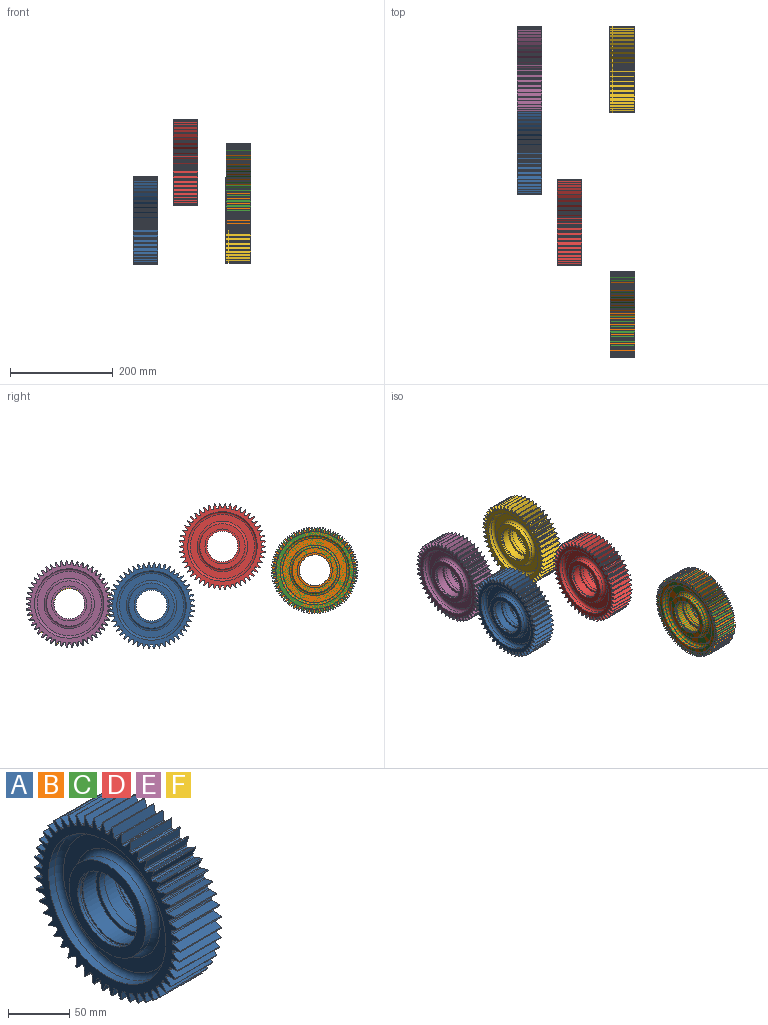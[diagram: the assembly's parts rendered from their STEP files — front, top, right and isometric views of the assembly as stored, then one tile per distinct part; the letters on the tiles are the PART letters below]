
ASSEMBLY  parts=6 mates=1
PART A: 327 faces, bbox 48x168x167.7 mm
  f0: plane 168x167.74mm, normal (-1,0,0), area 5101.1mm2, adj f1,f2,f3,f4,f5,f6,f7,f8
  f1: cylinder r=84mm len=48mm, axis (-1,0,0), area 45.2mm2, adj f0,f51,f122,f156
  f2: cylinder r=84mm len=48mm, axis (-1,0,0), area 43.9mm2, adj f0,f51,f151,f152
  f3: cylinder r=84mm len=48mm, axis (-1,0,0), area 42.7mm2, adj f0,f51,f147,f166
  f4: cylinder r=84mm len=48mm, axis (-1,0,0), area 41.5mm2, adj f0,f51,f161,f162
  f5: cylinder r=84mm len=48mm, axis (-1,0,0), area 40.5mm2, adj f0,f51,f136,f157
  f6: cylinder r=84mm len=48mm, axis (-1,0,0), area 39.7mm2, adj f0,f51,f131,f132
  f7: cylinder r=84mm len=48mm, axis (-1,0,0), area 39mm2, adj f0,f51,f127,f141
  f8: cylinder r=84mm len=48mm, axis (-1,0,0), area 38.4mm2, adj f0,f51,f137,f146
  f9: cylinder r=84mm len=48mm, axis (-1,0,0), area 38.1mm2, adj f0,f51,f86,f142
  f10: cylinder r=84mm len=48mm, axis (-1,0,0), area 37.9mm2, adj f0,f51,f80,f82
  f11: cylinder r=84mm len=48mm, axis (-1,0,0), area 38.1mm2, adj f0,f51,f207,f216
  f12: cylinder r=84mm len=48mm, axis (-1,0,0), area 38.4mm2, adj f0,f51,f212,f226
  f13: cylinder r=84mm len=48mm, axis (-1,0,0), area 39mm2, adj f0,f51,f221,f222
  f14: cylinder r=84mm len=48mm, axis (-1,0,0), area 39.7mm2, adj f0,f51,f217,f241
  f15: cylinder r=84mm len=48mm, axis (-1,0,0), area 40.6mm2, adj f0,f51,f237,f246
  f16: cylinder r=84mm len=48mm, axis (-1,0,0), area 41.6mm2, adj f0,f51,f231,f242
  f17: cylinder r=84mm len=48mm, axis (-1,0,0), area 42.7mm2, adj f0,f51,f227,f236
  f18: cylinder r=84mm len=48mm, axis (-1,0,0), area 43.9mm2, adj f0,f51,f206,f232
  f19: cylinder r=84mm len=48mm, axis (-1,0,0), area 45.2mm2, adj f0,f51,f201,f202
  f20: cylinder r=84mm len=48mm, axis (-1,0,0), area 46.6mm2, adj f0,f51,f196,f197
  f21: cylinder r=84mm len=48mm, axis (-1,0,0), area 48mm2, adj f0,f51,f191,f192
  f22: cylinder r=84mm len=48mm, axis (-1,0,0), area 49.5mm2, adj f0,f51,f186,f187
  f23: cylinder r=84mm len=48mm, axis (-1,0,0), area 50.9mm2, adj f0,f51,f181,f182
  f24: cylinder r=84mm len=48mm, axis (-1,0,0), area 52.4mm2, adj f0,f51,f171,f177
  f25: cylinder r=84mm len=48mm, axis (-1,0,0), area 53.8mm2, adj f0,f51,f167,f176
  f26: cylinder r=84mm len=48mm, axis (-1,0,0), area 55.1mm2, adj f0,f51,f172,f276
  f27: cylinder r=84mm len=48mm, axis (-1,0,0), area 56.3mm2, adj f0,f51,f271,f272
  f28: cylinder r=84mm len=48mm, axis (-1,0,0), area 57.4mm2, adj f0,f51,f267,f286
  f29: cylinder r=84mm len=48mm, axis (-1,0,0), area 58.4mm2, adj f0,f51,f281,f282
  f30: cylinder r=84mm len=48mm, axis (-1,0,0), area 59.3mm2, adj f0,f51,f261,f277
  f31: cylinder r=84mm len=48mm, axis (-1,0,0), area 60mm2, adj f0,f51,f257,f266
  f32: cylinder r=84mm len=48mm, axis (-1,0,0), area 60.5mm2, adj f0,f51,f256,f262
  f33: cylinder r=84mm len=48mm, axis (-1,0,0), area 60.8mm2, adj f0,f51,f251,f252
  f34: cylinder r=84mm len=48mm, axis (-1,0,0), area 61mm2, adj f0,f51,f247,f326
  f35: cylinder r=84mm len=48mm, axis (-1,0,0), area 61mm2, adj f0,f51,f321,f322
  f36: cylinder r=84mm len=48mm, axis (-1,0,0), area 60.8mm2, adj f0,f51,f316,f317
  f37: cylinder r=84mm len=48mm, axis (-1,0,0), area 60.5mm2, adj f0,f51,f311,f312
  f38: cylinder r=84mm len=48mm, axis (-1,0,0), area 59.9mm2, adj f0,f51,f296,f307
  f39: cylinder r=84mm len=48mm, axis (-1,0,0), area 59.2mm2, adj f0,f51,f291,f292
  f40: cylinder r=84mm len=48mm, axis (-1,0,0), area 58.4mm2, adj f0,f51,f287,f306
  f41: cylinder r=84mm len=48mm, axis (-1,0,0), area 57.4mm2, adj f0,f51,f301,f302
  f42: cylinder r=84mm len=48mm, axis (-1,0,0), area 56.3mm2, adj f0,f51,f96,f297
  f43: cylinder r=84mm len=48mm, axis (-1,0,0), area 55.1mm2, adj f0,f51,f91,f92
  f44: cylinder r=84mm len=48mm, axis (-1,0,0), area 53.7mm2, adj f0,f51,f87,f101
  f45: cylinder r=84mm len=48mm, axis (-1,0,0), area 52.4mm2, adj f0,f51,f97,f106
  f46: cylinder r=84mm len=48mm, axis (-1,0,0), area 50.9mm2, adj f0,f51,f102,f111
  f47: cylinder r=84mm len=48mm, axis (-1,0,0), area 49.5mm2, adj f0,f51,f107,f116
  f48: cylinder r=84mm len=48mm, axis (-1,0,0), area 48mm2, adj f0,f51,f112,f121
  f49: cylinder r=84mm len=48mm, axis (-1,0,0), area 46.6mm2, adj f0,f51,f117,f126
  f50: cylinder r=84mm len=48mm, axis (-1,0,0), area 37.9mm2, adj f0,f51,f81,f211
  f51: plane 168x167.74mm, normal (1,0,0), area 5101.1mm2, adj f1,f2,f3,f4,f5,f6,f7,f8
  f52: cylinder r=44mm len=88mm, axis (-1,0,0), area 1935.2mm2, adj f53,f76
  f53: plane 88x88mm, normal (-1,0,0), area 2450.4mm2, adj f52,f54
  f54: cylinder r=34mm len=68mm, axis (-1,0,0), area 640.9mm2, adj f53,f55
  f55: plane 71x71mm, normal (1,0,0), area 327.5mm2, adj f54,f56
  f56: cylinder r=35.5mm len=71mm, axis (-1,0,0), area 669.2mm2, adj f55,f57
  f57: plane 71x71mm, normal (-1,0,0), area 327.5mm2, adj f56,f58
  f58: cylinder r=34mm len=68mm, axis (-1,0,0), area 3204.4mm2, adj f57,f59
  f59: plane 68x68mm, normal (-1,0,0), area 804.2mm2, adj f58,f60
  f60: cylinder r=30mm len=60mm, axis (-1,0,0), area 1131mm2, adj f59,f61
  f61: plane 68x68mm, normal (1,0,0), area 804.2mm2, adj f60,f62
  f62: cylinder r=34mm len=68mm, axis (-1,0,0), area 3204.4mm2, adj f61,f63
  f63: plane 71x71mm, normal (1,0,0), area 327.5mm2, adj f62,f64
  f64: cylinder r=35.5mm len=71mm, axis (-1,0,0), area 669.2mm2, adj f63,f65
  f65: plane 71x71mm, normal (-1,0,0), area 327.5mm2, adj f64,f66
  f66: cylinder r=34mm len=68mm, axis (-1,0,0), area 640.9mm2, adj f65,f67
  f67: plane 88x88mm, normal (1,0,0), area 2450.4mm2, adj f66,f68
  f68: cylinder r=44mm len=88mm, axis (-1,0,0), area 2535.7mm2, adj f67,f69
  f69: torus R=46.83mm, axis (-1,0,0), area 1256.8mm2, adj f68,f70
  f70: plane 125x125mm, normal (1,0,0), area 5382.8mm2, adj f69,f71
  f71: torus R=62.5mm, axis (-1,0,0), area 3241.3mm2, adj f70,f72
  f72: cylinder r=67.5mm len=135mm, axis (-1,0,0), area 2968.8mm2, adj f51,f71
  f73: cylinder r=67.5mm len=135mm, axis (-1,0,0), area 2968.8mm2, adj f0,f74
  f74: torus R=62.5mm, axis (-1,0,0), area 3241.3mm2, adj f73,f75
  f75: plane 125x125mm, normal (-1,0,0), area 4728.9mm2, adj f74,f76
  f76: torus R=49mm, axis (-1,0,0), area 2261mm2, adj f52,f75
  f77: cylinder r=1mm len=48mm, axis (-1,0,0), area 58.6mm2, adj f0,f51,f78,f81
  f78: plane 48x1.77mm, normal (0,0,1), area 84.8mm2, adj f0,f51,f77,f79
  f79: cylinder r=1mm len=48mm, axis (-1,0,0), area 58.8mm2, adj f0,f51,f78,f80
  f80: plane 48x8.31mm, normal (0,-0.94,0.34), area 423.7mm2, adj f0,f10,f51,f79
  f81: plane 48x8.3mm, normal (0,0.93,0.36), area 426.6mm2, adj f0,f50,f51,f77
  f82: plane 48x8.63mm, normal (0,0.97,0.24), area 426.6mm2, adj f0,f10,f51,f83
  f83: cylinder r=1mm len=48mm, axis (-1,0,0), area 58.6mm2, adj f0,f51,f82,f84
  f84: plane 48x1.75mm, normal (0,0.13,0.99), area 84.8mm2, adj f0,f51,f83,f85
  f85: cylinder r=1mm len=48mm, axis (-1,0,0), area 58.8mm2, adj f0,f51,f84,f86
  f86: plane 48x7.86mm, normal (0,-0.89,0.45), area 423.4mm2, adj f0,f9,f51,f85
  f87: plane 48x8.29mm, normal (0,-0.07,-1), area 398.9mm2, adj f0,f44,f51,f88
  f88: cylinder r=1mm len=48mm, axis (-1,0,0), area 58.6mm2, adj f0,f51,f87,f89
  f89: plane 48x1.6mm, normal (0,0.9,-0.43), area 84.8mm2, adj f0,f51,f88,f90
  f90: cylinder r=1mm len=48mm, axis (-1,0,0), area 58.8mm2, adj f0,f51,f89,f91
  f91: plane 48x5.81mm, normal (0,0.71,0.71), area 394.2mm2, adj f0,f43,f51,f90
  f92: plane 48x8.1mm, normal (0,-0.2,-0.98), area 396.6mm2, adj f0,f43,f51,f93
  f93: cylinder r=1mm len=48mm, axis (-1,0,0), area 58.6mm2, adj f0,f51,f92,f94
  f94: plane 48x1.49mm, normal (0,0.84,-0.54), area 84.8mm2, adj f0,f51,f93,f95
  f95: cylinder r=1mm len=48mm, axis (-1,0,0), area 58.8mm2, adj f0,f51,f94,f96
  f96: plane 48x6.45mm, normal (0,0.79,0.61), area 392mm2, adj f0,f42,f51,f95
  f97: plane 48x8.35mm, normal (0,0.05,-1), area 401.3mm2, adj f0,f45,f51,f98
  f98: cylinder r=1mm len=48mm, axis (-1,0,0), area 58.6mm2, adj f0,f51,f97,f99
  f99: plane 48x1.68mm, normal (0,0.95,-0.31), area 84.8mm2, adj f0,f51,f98,f100
  f100: cylinder r=1mm len=48mm, axis (-1,0,0), area 58.8mm2, adj f0,f51,f99,f101
  f101: plane 48x6.53mm, normal (0,0.61,0.79), area 396.4mm2, adj f0,f44,f51,f100
  f102: plane 48x8.28mm, normal (0,0.18,-0.98), area 403.8mm2, adj f0,f46,f51,f103
  f103: cylinder r=1mm len=48mm, axis (-1,0,0), area 58.6mm2, adj f0,f51,f102,f104
  f104: plane 48x1.74mm, normal (0,0.98,-0.19), area 84.8mm2, adj f0,f51,f103,f105
  f105: cylinder r=1mm len=48mm, axis (-1,0,0), area 58.8mm2, adj f0,f51,f104,f106
  f106: plane 48x7.15mm, normal (0,0.51,0.86), area 398.8mm2, adj f0,f45,f51,f105
  f107: plane 48x8.08mm, normal (0,0.3,-0.95), area 406.3mm2, adj f0,f47,f51,f108
  f108: cylinder r=1mm len=48mm, axis (-1,0,0), area 58.6mm2, adj f0,f51,f107,f109
  f109: plane 48x1.76mm, normal (0,1,-0.06), area 84.8mm2, adj f0,f51,f108,f110
  f110: cylinder r=1mm len=48mm, axis (-1,0,0), area 58.8mm2, adj f0,f51,f109,f111
  f111: plane 48x7.67mm, normal (0,0.4,0.92), area 401.3mm2, adj f0,f46,f51,f110
  f112: plane 48x7.75mm, normal (0,0.42,-0.91), area 408.9mm2, adj f0,f48,f51,f113
  f113: cylinder r=1mm len=48mm, axis (-1,0,0), area 58.6mm2, adj f0,f51,f112,f114
  f114: plane 48x1.76mm, normal (0,1,0.06), area 84.8mm2, adj f0,f51,f113,f115
  f115: cylinder r=1mm len=48mm, axis (-1,0,0), area 58.8mm2, adj f0,f51,f114,f116
  f116: plane 48x8.08mm, normal (0,0.28,0.96), area 403.8mm2, adj f0,f47,f51,f115
  f117: plane 48x7.29mm, normal (0,0.53,-0.85), area 411.4mm2, adj f0,f49,f51,f118
  f118: cylinder r=1mm len=48mm, axis (-1,0,0), area 58.6mm2, adj f0,f51,f117,f119
  f119: plane 48x1.74mm, normal (0,0.98,0.19), area 84.8mm2, adj f0,f51,f118,f120
  f120: cylinder r=1mm len=48mm, axis (-1,0,0), area 58.8mm2, adj f0,f51,f119,f121
  f121: plane 48x8.36mm, normal (0,0.16,0.99), area 406.3mm2, adj f0,f48,f51,f120
  f122: plane 48x6.7mm, normal (0,0.63,-0.78), area 413.8mm2, adj f0,f1,f51,f123
  f123: cylinder r=1mm len=48mm, axis (-1,0,0), area 58.6mm2, adj f0,f51,f122,f124
  f124: plane 48x1.68mm, normal (0,0.95,0.31), area 84.8mm2, adj f0,f51,f123,f125
  f125: cylinder r=1mm len=48mm, axis (-1,0,0), area 58.8mm2, adj f0,f51,f124,f126
  f126: plane 48x8.51mm, normal (0,0.03,1), area 408.8mm2, adj f0,f49,f51,f125
  f127: plane 48x8.76mm, normal (0,0.99,-0.14), area 424.7mm2, adj f0,f7,f51,f128
  f128: cylinder r=1mm len=48mm, axis (-1,0,0), area 58.6mm2, adj f0,f51,f127,f129
  f129: plane 48x1.55mm, normal (0,0.48,0.88), area 84.8mm2, adj f0,f51,f128,f130
  f130: cylinder r=1mm len=48mm, axis (-1,0,0), area 58.8mm2, adj f0,f51,f129,f131
  f131: plane 48x6.57mm, normal (0,-0.66,0.75), area 420.7mm2, adj f0,f6,f51,f130
  f132: plane 48x8.52mm, normal (0,0.97,-0.26), area 423.4mm2, adj f0,f6,f51,f133
  f133: cylinder r=1mm len=48mm, axis (-1,0,0), area 58.6mm2, adj f0,f51,f132,f134
  f134: plane 48x1.43mm, normal (0,0.59,0.81), area 84.8mm2, adj f0,f51,f133,f135
  f135: cylinder r=1mm len=48mm, axis (-1,0,0), area 58.8mm2, adj f0,f51,f134,f136
  f136: plane 48x7.22mm, normal (0,-0.56,0.83), area 419.2mm2, adj f0,f5,f51,f135
  f137: plane 48x8.87mm, normal (0,1,-0.01), area 425.6mm2, adj f0,f8,f51,f138
  f138: cylinder r=1mm len=48mm, axis (-1,0,0), area 58.6mm2, adj f0,f51,f137,f139
  f139: plane 48x1.64mm, normal (0,0.37,0.93), area 84.8mm2, adj f0,f51,f138,f140
  f140: cylinder r=1mm len=48mm, axis (-1,0,0), area 58.8mm2, adj f0,f51,f139,f141
  f141: plane 48x6.6mm, normal (0,-0.75,0.66), area 421.9mm2, adj f0,f7,f51,f140
  f142: plane 48x8.82mm, normal (0,0.99,0.11), area 426.3mm2, adj f0,f9,f51,f143
  f143: cylinder r=1mm len=48mm, axis (-1,0,0), area 58.6mm2, adj f0,f51,f142,f144
  f144: plane 48x1.71mm, normal (0,0.25,0.97), area 84.8mm2, adj f0,f51,f143,f145
  f145: cylinder r=1mm len=48mm, axis (-1,0,0), area 58.8mm2, adj f0,f51,f144,f146
  f146: plane 48x7.29mm, normal (0,-0.83,0.56), area 422.8mm2, adj f0,f8,f51,f145
  f147: plane 48x6.99mm, normal (0,0.8,-0.6), area 418.2mm2, adj f0,f3,f51,f148
  f148: cylinder r=1mm len=48mm, axis (-1,0,0), area 58.6mm2, adj f0,f51,f147,f149
  f149: plane 48x1.49mm, normal (0,0.84,0.54), area 84.8mm2, adj f0,f51,f148,f150
  f150: cylinder r=1mm len=48mm, axis (-1,0,0), area 58.8mm2, adj f0,f51,f149,f151
  f151: plane 48x8.41mm, normal (0,-0.22,0.98), area 413.4mm2, adj f0,f2,f51,f150
  f152: plane 48x6.25mm, normal (0,0.72,-0.69), area 416.1mm2, adj f0,f2,f51,f153
  f153: cylinder r=1mm len=48mm, axis (-1,0,0), area 58.6mm2, adj f0,f51,f152,f154
  f154: plane 48x1.6mm, normal (0,0.9,0.43), area 84.8mm2, adj f0,f51,f153,f155
  f155: cylinder r=1mm len=48mm, axis (-1,0,0), area 58.8mm2, adj f0,f51,f154,f156
  f156: plane 48x8.53mm, normal (0,-0.09,1), area 411.2mm2, adj f0,f1,f51,f155
  f157: plane 48x8.14mm, normal (0,0.93,-0.38), area 421.9mm2, adj f0,f5,f51,f158
  f158: cylinder r=1mm len=48mm, axis (-1,0,0), area 58.6mm2, adj f0,f51,f157,f159
  f159: plane 48x1.29mm, normal (0,0.68,0.73), area 84.8mm2, adj f0,f51,f158,f160
  f160: cylinder r=1mm len=48mm, axis (-1,0,0), area 58.8mm2, adj f0,f51,f159,f161
  f161: plane 48x7.75mm, normal (0,-0.45,0.89), area 417.5mm2, adj f0,f4,f51,f160
  f162: plane 48x7.62mm, normal (0,0.87,-0.49), area 420.2mm2, adj f0,f4,f51,f163
  f163: cylinder r=1mm len=48mm, axis (-1,0,0), area 58.6mm2, adj f0,f51,f162,f164
  f164: plane 48x1.36mm, normal (0,0.77,0.64), area 84.8mm2, adj f0,f51,f163,f165
  f165: cylinder r=1mm len=48mm, axis (-1,0,0), area 58.8mm2, adj f0,f51,f164,f166
  f166: plane 48x8.14mm, normal (0,-0.34,0.94), area 415.6mm2, adj f0,f3,f51,f165
  f167: plane 48x6.47mm, normal (0,-0.63,0.78), area 399.1mm2, adj f0,f25,f51,f168
  f168: cylinder r=1mm len=48mm, axis (-1,0,0), area 58.6mm2, adj f0,f51,f167,f169
  f169: plane 48x1.68mm, normal (0,-0.95,-0.31), area 84.8mm2, adj f0,f51,f168,f170
  f170: cylinder r=1mm len=48mm, axis (-1,0,0), area 58.8mm2, adj f0,f51,f169,f171
  f171: plane 48x8.3mm, normal (0,-0.03,-1), area 398.6mm2, adj f0,f24,f51,f170
  f172: plane 48x5.96mm, normal (0,-0.72,0.69), area 396.8mm2, adj f0,f26,f51,f173
  f173: cylinder r=1mm len=48mm, axis (-1,0,0), area 58.6mm2, adj f0,f51,f172,f174
  f174: plane 48x1.6mm, normal (0,-0.9,-0.43), area 84.8mm2, adj f0,f51,f173,f175
  f175: cylinder r=1mm len=48mm, axis (-1,0,0), area 58.8mm2, adj f0,f51,f174,f176
  f176: plane 48x8.22mm, normal (0,0.09,-1), area 396.2mm2, adj f0,f25,f51,f175
  f177: plane 48x7.11mm, normal (0,-0.53,0.85), area 401.5mm2, adj f0,f24,f51,f178
  f178: cylinder r=1mm len=48mm, axis (-1,0,0), area 58.6mm2, adj f0,f51,f177,f179
  f179: plane 48x1.74mm, normal (0,-0.98,-0.19), area 84.8mm2, adj f0,f51,f178,f180
  f180: cylinder r=1mm len=48mm, axis (-1,0,0), area 58.8mm2, adj f0,f51,f179,f181
  f181: plane 48x8.25mm, normal (0,-0.16,-0.99), area 401mm2, adj f0,f23,f51,f180
  f182: plane 48x7.66mm, normal (0,-0.42,0.91), area 404mm2, adj f0,f23,f51,f183
  f183: cylinder r=1mm len=48mm, axis (-1,0,0), area 58.6mm2, adj f0,f51,f182,f184
  f184: plane 48x1.76mm, normal (0,-1,-0.06), area 84.8mm2, adj f0,f51,f183,f185
  f185: cylinder r=1mm len=48mm, axis (-1,0,0), area 58.8mm2, adj f0,f51,f184,f186
  f186: plane 48x8.07mm, normal (0,-0.28,-0.96), area 403.5mm2, adj f0,f22,f51,f185
  f187: plane 48x8.08mm, normal (0,-0.3,0.95), area 406.5mm2, adj f0,f22,f51,f188
  f188: cylinder r=1mm len=48mm, axis (-1,0,0), area 58.6mm2, adj f0,f51,f187,f189
  f189: plane 48x1.76mm, normal (0,-1,0.06), area 84.8mm2, adj f0,f51,f188,f190
  f190: cylinder r=1mm len=48mm, axis (-1,0,0), area 58.8mm2, adj f0,f51,f189,f191
  f191: plane 48x7.77mm, normal (0,-0.4,-0.92), area 406mm2, adj f0,f21,f51,f190
  f192: plane 48x8.39mm, normal (0,-0.18,0.98), area 409.1mm2, adj f0,f21,f51,f193
  f193: cylinder r=1mm len=48mm, axis (-1,0,0), area 58.6mm2, adj f0,f51,f192,f194
  f194: plane 48x1.74mm, normal (0,-0.98,0.19), area 84.8mm2, adj f0,f51,f193,f195
  f195: cylinder r=1mm len=48mm, axis (-1,0,0), area 58.8mm2, adj f0,f51,f194,f196
  f196: plane 48x7.33mm, normal (0,-0.51,-0.86), area 408.5mm2, adj f0,f20,f51,f195
  f197: plane 48x8.56mm, normal (0,-0.05,1), area 411.5mm2, adj f0,f20,f51,f198
  f198: cylinder r=1mm len=48mm, axis (-1,0,0), area 58.6mm2, adj f0,f51,f197,f199
  f199: plane 48x1.68mm, normal (0,-0.95,0.31), area 84.8mm2, adj f0,f51,f198,f200
  f200: cylinder r=1mm len=48mm, axis (-1,0,0), area 58.8mm2, adj f0,f51,f199,f201
  f201: plane 48x6.77mm, normal (0,-0.61,-0.79), area 410.9mm2, adj f0,f19,f51,f200
  f202: plane 48x8.6mm, normal (0,0.07,1), area 413.9mm2, adj f0,f19,f51,f203
  f203: cylinder r=1mm len=48mm, axis (-1,0,0), area 58.6mm2, adj f0,f51,f202,f204
  f204: plane 48x1.6mm, normal (0,-0.9,0.43), area 84.8mm2, adj f0,f51,f203,f205
  f205: cylinder r=1mm len=48mm, axis (-1,0,0), area 58.8mm2, adj f0,f51,f204,f206
  f206: plane 48x6.09mm, normal (0,-0.71,-0.71), area 413.2mm2, adj f0,f18,f51,f205
  f207: plane 48x7.83mm, normal (0,0.88,0.47), area 426.3mm2, adj f0,f11,f51,f208
  f208: cylinder r=1mm len=48mm, axis (-1,0,0), area 58.6mm2, adj f0,f51,f207,f209
  f209: plane 48x1.75mm, normal (0,-0.13,0.99), area 84.8mm2, adj f0,f51,f208,f210
  f210: cylinder r=1mm len=48mm, axis (-1,0,0), area 58.8mm2, adj f0,f51,f209,f211
  f211: plane 48x8.62mm, normal (0,-0.98,0.22), area 423.7mm2, adj f0,f50,f51,f210
  f212: plane 48x7.23mm, normal (0,0.82,0.58), area 425.7mm2, adj f0,f12,f51,f213
  f213: cylinder r=1mm len=48mm, axis (-1,0,0), area 58.6mm2, adj f0,f51,f212,f214
  f214: plane 48x1.71mm, normal (0,-0.25,0.97), area 84.8mm2, adj f0,f51,f213,f215
  f215: cylinder r=1mm len=48mm, axis (-1,0,0), area 58.8mm2, adj f0,f51,f214,f216
  f216: plane 48x8.78mm, normal (0,-1,0.09), area 423.4mm2, adj f0,f11,f51,f215
  f217: plane 48x6.73mm, normal (0,0.65,0.76), area 423.5mm2, adj f0,f14,f51,f218
  f218: cylinder r=1mm len=48mm, axis (-1,0,0), area 58.6mm2, adj f0,f51,f217,f219
  f219: plane 48x1.55mm, normal (0,-0.48,0.88), area 84.8mm2, adj f0,f51,f218,f220
  f220: cylinder r=1mm len=48mm, axis (-1,0,0), area 58.8mm2, adj f0,f51,f219,f221
  f221: plane 48x8.68mm, normal (0,-0.99,-0.16), area 421.8mm2, adj f0,f13,f51,f220
  f222: plane 48x6.52mm, normal (0,0.74,0.68), area 424.7mm2, adj f0,f13,f51,f223
  f223: cylinder r=1mm len=48mm, axis (-1,0,0), area 58.6mm2, adj f0,f51,f222,f224
  f224: plane 48x1.64mm, normal (0,-0.37,0.93), area 84.8mm2, adj f0,f51,f223,f225
  f225: cylinder r=1mm len=48mm, axis (-1,0,0), area 58.8mm2, adj f0,f51,f224,f226
  f226: plane 48x8.8mm, normal (0,-1,-0.03), area 422.7mm2, adj f0,f12,f51,f225
  f227: plane 48x8.26mm, normal (0,0.32,0.95), area 418.4mm2, adj f0,f17,f51,f228
  f228: cylinder r=1mm len=48mm, axis (-1,0,0), area 58.6mm2, adj f0,f51,f227,f229
  f229: plane 48x1.36mm, normal (0,-0.77,0.64), area 84.8mm2, adj f0,f51,f228,f230
  f230: cylinder r=1mm len=48mm, axis (-1,0,0), area 58.8mm2, adj f0,f51,f229,f231
  f231: plane 48x7.48mm, normal (0,-0.86,-0.51), area 417.3mm2, adj f0,f16,f51,f230
  f232: plane 48x8.5mm, normal (0,0.2,0.98), area 416.2mm2, adj f0,f18,f51,f233
  f233: cylinder r=1mm len=48mm, axis (-1,0,0), area 58.6mm2, adj f0,f51,f232,f234
  f234: plane 48x1.49mm, normal (0,-0.84,0.54), area 84.8mm2, adj f0,f51,f233,f235
  f235: cylinder r=1mm len=48mm, axis (-1,0,0), area 58.8mm2, adj f0,f51,f234,f236
  f236: plane 48x6.83mm, normal (0,-0.79,-0.61), area 415.4mm2, adj f0,f17,f51,f235
  f237: plane 48x7.37mm, normal (0,0.55,0.84), area 422mm2, adj f0,f15,f51,f238
  f238: cylinder r=1mm len=48mm, axis (-1,0,0), area 58.6mm2, adj f0,f51,f237,f239
  f239: plane 48x1.43mm, normal (0,-0.59,0.81), area 84.8mm2, adj f0,f51,f238,f240
  f240: cylinder r=1mm len=48mm, axis (-1,0,0), area 58.8mm2, adj f0,f51,f239,f241
  f241: plane 48x8.41mm, normal (0,-0.96,-0.28), area 420.6mm2, adj f0,f14,f51,f240
  f242: plane 48x7.88mm, normal (0,0.44,0.9), area 420.3mm2, adj f0,f16,f51,f243
  f243: cylinder r=1mm len=48mm, axis (-1,0,0), area 58.6mm2, adj f0,f51,f242,f244
  f244: plane 48x1.29mm, normal (0,-0.68,0.73), area 84.8mm2, adj f0,f51,f243,f245
  f245: cylinder r=1mm len=48mm, axis (-1,0,0), area 58.8mm2, adj f0,f51,f244,f246
  f246: plane 48x8.01mm, normal (0,-0.92,-0.4), area 419.1mm2, adj f0,f15,f51,f245
  f247: plane 48x7.82mm, normal (0,-0.97,-0.24), area 386.4mm2, adj f0,f34,f51,f248
  f248: cylinder r=1mm len=48mm, axis (-1,0,0), area 58.6mm2, adj f0,f51,f247,f249
  f249: plane 48x1.75mm, normal (0,-0.13,-0.99), area 84.8mm2, adj f0,f51,f248,f250
  f250: cylinder r=1mm len=48mm, axis (-1,0,0), area 58.8mm2, adj f0,f51,f249,f251
  f251: plane 48x7.13mm, normal (0,0.89,-0.45), area 384mm2, adj f0,f33,f51,f250
  f252: plane 48x8mm, normal (0,-0.99,-0.11), area 386.7mm2, adj f0,f33,f51,f253
  f253: cylinder r=1mm len=48mm, axis (-1,0,0), area 58.6mm2, adj f0,f51,f252,f254
  f254: plane 48x1.71mm, normal (0,-0.25,-0.97), area 84.8mm2, adj f0,f51,f253,f255
  f255: cylinder r=1mm len=48mm, axis (-1,0,0), area 58.8mm2, adj f0,f51,f254,f256
  f256: plane 48x6.63mm, normal (0,0.83,-0.56), area 384.6mm2, adj f0,f32,f51,f255
  f257: plane 48x8.01mm, normal (0,-0.99,0.14), area 388.3mm2, adj f0,f31,f51,f258
  f258: cylinder r=1mm len=48mm, axis (-1,0,0), area 58.6mm2, adj f0,f51,f257,f259
  f259: plane 48x1.55mm, normal (0,-0.48,-0.88), area 84.8mm2, adj f0,f51,f258,f260
  f260: cylinder r=1mm len=48mm, axis (-1,0,0), area 58.8mm2, adj f0,f51,f259,f261
  f261: plane 48x6.04mm, normal (0,0.66,-0.75), area 386.7mm2, adj f0,f30,f51,f260
  f262: plane 48x8.07mm, normal (0,-1,0.01), area 387.4mm2, adj f0,f32,f51,f263
  f263: cylinder r=1mm len=48mm, axis (-1,0,0), area 58.6mm2, adj f0,f51,f262,f264
  f264: plane 48x1.64mm, normal (0,-0.37,-0.93), area 84.8mm2, adj f0,f51,f263,f265
  f265: cylinder r=1mm len=48mm, axis (-1,0,0), area 58.8mm2, adj f0,f51,f264,f266
  f266: plane 48x6.03mm, normal (0,0.75,-0.66), area 385.5mm2, adj f0,f31,f51,f265
  f267: plane 48x7.13mm, normal (0,-0.87,0.49), area 392.8mm2, adj f0,f28,f51,f268
  f268: cylinder r=1mm len=48mm, axis (-1,0,0), area 58.6mm2, adj f0,f51,f267,f269
  f269: plane 48x1.36mm, normal (0,-0.77,-0.64), area 84.8mm2, adj f0,f51,f268,f270
  f270: cylinder r=1mm len=48mm, axis (-1,0,0), area 58.8mm2, adj f0,f51,f269,f271
  f271: plane 48x7.68mm, normal (0,0.34,-0.94), area 391.8mm2, adj f0,f27,f51,f270
  f272: plane 48x6.6mm, normal (0,-0.8,0.6), area 394.7mm2, adj f0,f27,f51,f273
  f273: cylinder r=1mm len=48mm, axis (-1,0,0), area 58.6mm2, adj f0,f51,f272,f274
  f274: plane 48x1.49mm, normal (0,-0.84,-0.54), area 84.8mm2, adj f0,f51,f273,f275
  f275: cylinder r=1mm len=48mm, axis (-1,0,0), area 58.8mm2, adj f0,f51,f274,f276
  f276: plane 48x8.01mm, normal (0,0.22,-0.98), area 393.9mm2, adj f0,f26,f51,f275
  f277: plane 48x7.84mm, normal (0,-0.97,0.26), area 389.5mm2, adj f0,f30,f51,f278
  f278: cylinder r=1mm len=48mm, axis (-1,0,0), area 58.6mm2, adj f0,f51,f277,f279
  f279: plane 48x1.43mm, normal (0,-0.59,-0.81), area 84.8mm2, adj f0,f51,f278,f280
  f280: cylinder r=1mm len=48mm, axis (-1,0,0), area 58.8mm2, adj f0,f51,f279,f281
  f281: plane 48x6.69mm, normal (0,0.56,-0.83), area 388.2mm2, adj f0,f29,f51,f280
  f282: plane 48x7.54mm, normal (0,-0.93,0.38), area 391mm2, adj f0,f29,f51,f283
  f283: cylinder r=1mm len=48mm, axis (-1,0,0), area 58.6mm2, adj f0,f51,f282,f284
  f284: plane 48x1.29mm, normal (0,-0.68,-0.73), area 84.8mm2, adj f0,f51,f283,f285
  f285: cylinder r=1mm len=48mm, axis (-1,0,0), area 58.8mm2, adj f0,f51,f284,f286
  f286: plane 48x7.24mm, normal (0,0.45,-0.89), area 389.9mm2, adj f0,f28,f51,f285
  f287: plane 48x6.83mm, normal (0,-0.55,-0.84), area 390.9mm2, adj f0,f40,f51,f288
  f288: cylinder r=1mm len=48mm, axis (-1,0,0), area 58.6mm2, adj f0,f51,f287,f289
  f289: plane 48x1.43mm, normal (0,0.59,-0.81), area 84.8mm2, adj f0,f51,f288,f290
  f290: cylinder r=1mm len=48mm, axis (-1,0,0), area 58.8mm2, adj f0,f51,f289,f291
  f291: plane 48x7.74mm, normal (0,0.96,0.28), area 386.9mm2, adj f0,f39,f51,f290
  f292: plane 48x6.19mm, normal (0,-0.65,-0.76), area 389.4mm2, adj f0,f39,f51,f293
  f293: cylinder r=1mm len=48mm, axis (-1,0,0), area 58.6mm2, adj f0,f51,f292,f294
  f294: plane 48x1.55mm, normal (0,0.48,-0.88), area 84.8mm2, adj f0,f51,f293,f295
  f295: cylinder r=1mm len=48mm, axis (-1,0,0), area 58.8mm2, adj f0,f51,f294,f296
  f296: plane 48x7.94mm, normal (0,0.99,0.16), area 385.7mm2, adj f0,f38,f51,f295
  f297: plane 48x7.79mm, normal (0,-0.32,-0.95), area 394.5mm2, adj f0,f42,f51,f298
  f298: cylinder r=1mm len=48mm, axis (-1,0,0), area 58.6mm2, adj f0,f51,f297,f299
  f299: plane 48x1.36mm, normal (0,0.77,-0.64), area 84.8mm2, adj f0,f51,f298,f300
  f300: cylinder r=1mm len=48mm, axis (-1,0,0), area 58.8mm2, adj f0,f51,f299,f301
  f301: plane 48x6.99mm, normal (0,0.86,0.51), area 390.1mm2, adj f0,f41,f51,f300
  f302: plane 48x7.36mm, normal (0,-0.44,-0.9), area 392.6mm2, adj f0,f41,f51,f303
  f303: cylinder r=1mm len=48mm, axis (-1,0,0), area 58.6mm2, adj f0,f51,f302,f304
  f304: plane 48x1.29mm, normal (0,0.68,-0.73), area 84.8mm2, adj f0,f51,f303,f305
  f305: cylinder r=1mm len=48mm, axis (-1,0,0), area 58.8mm2, adj f0,f51,f304,f306
  f306: plane 48x7.42mm, normal (0,0.92,0.4), area 388.4mm2, adj f0,f40,f51,f305
  f307: plane 48x5.96mm, normal (0,-0.74,-0.68), area 388.2mm2, adj f0,f38,f51,f308
  f308: cylinder r=1mm len=48mm, axis (-1,0,0), area 58.6mm2, adj f0,f51,f307,f309
  f309: plane 48x1.64mm, normal (0,0.37,-0.93), area 84.8mm2, adj f0,f51,f308,f310
  f310: cylinder r=1mm len=48mm, axis (-1,0,0), area 58.8mm2, adj f0,f51,f309,f311
  f311: plane 48x8.01mm, normal (0,1,0.03), area 384.7mm2, adj f0,f37,f51,f310
  f312: plane 48x6.58mm, normal (0,-0.82,-0.58), area 387.3mm2, adj f0,f37,f51,f313
  f313: cylinder r=1mm len=48mm, axis (-1,0,0), area 58.6mm2, adj f0,f51,f312,f314
  f314: plane 48x1.71mm, normal (0,0.25,-0.97), area 84.8mm2, adj f0,f51,f313,f315
  f315: cylinder r=1mm len=48mm, axis (-1,0,0), area 58.8mm2, adj f0,f51,f314,f316
  f316: plane 48x7.97mm, normal (0,1,-0.09), area 384.1mm2, adj f0,f36,f51,f315
  f317: plane 48x7.1mm, normal (0,-0.88,-0.47), area 386.7mm2, adj f0,f36,f51,f318
  f318: cylinder r=1mm len=48mm, axis (-1,0,0), area 58.6mm2, adj f0,f51,f317,f319
  f319: plane 48x1.75mm, normal (0,0.13,-0.99), area 84.8mm2, adj f0,f51,f318,f320
  f320: cylinder r=1mm len=48mm, axis (-1,0,0), area 58.8mm2, adj f0,f51,f319,f321
  f321: plane 48x7.8mm, normal (0,0.98,-0.22), area 383.7mm2, adj f0,f35,f51,f320
  f322: plane 48x7.52mm, normal (0,-0.93,-0.36), area 386.4mm2, adj f0,f35,f51,f323
  f323: cylinder r=1mm len=48mm, axis (-1,0,0), area 58.6mm2, adj f0,f51,f322,f324
  f324: plane 48x1.77mm, normal (0,0,-1), area 84.8mm2, adj f0,f51,f323,f325
  f325: cylinder r=1mm len=48mm, axis (-1,0,0), area 58.8mm2, adj f0,f51,f324,f326
  f326: plane 48x7.52mm, normal (0,0.94,-0.34), area 383.7mm2, adj f0,f34,f51,f325
PART B: same geometry as A
PART C: same geometry as A
PART D: same geometry as A
PART E: same geometry as A
PART F: same geometry as A
PLACE A t=(-7.34,-40.04,15.09)mm
PLACE B rot(axis=(1,0,0),90deg) t=(173.65,-387.48,53.72)mm
PLACE C t=(173.65,-357.48,83.72)mm
PLACE D t=(70.26,-177.94,130.02)mm
PLACE E t=(-7.63,120.03,19.15)mm
PLACE F t=(172.95,119.34,17.64)mm
MATE revolute B.f1 <-> C.f1  axis (1,0,0) through (176.65,-357.48,53.72)mm
